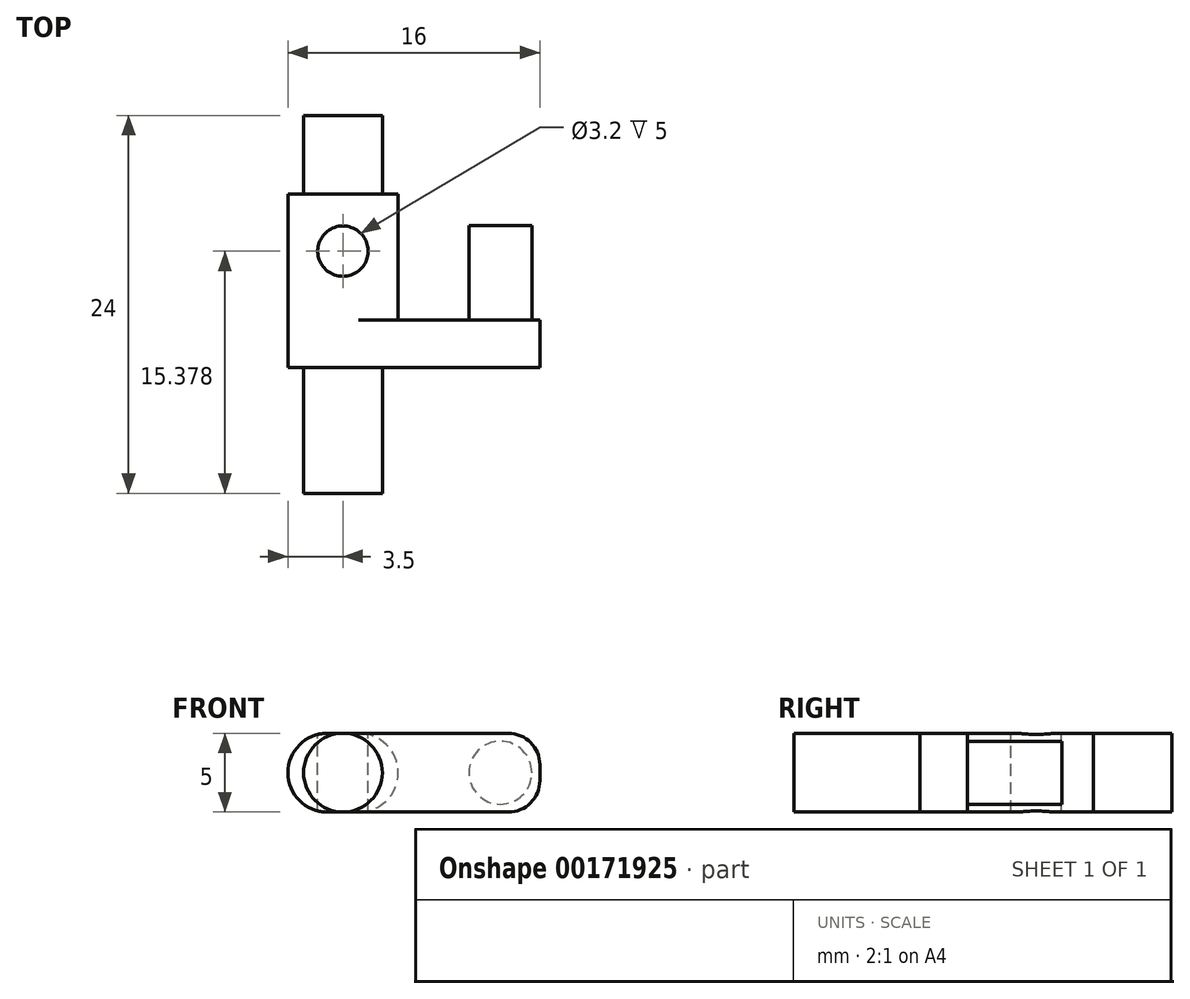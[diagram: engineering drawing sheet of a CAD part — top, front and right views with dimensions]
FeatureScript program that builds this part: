
annotation { "Feature Type Name" : "Feature", "Feature Type Description" : "" }
export const myFeature = defineFeature(function(context is Context, id is Id, definition is map)
    precondition{}
    {
        {
            var Q0;
            Q0=qCreatedBy(makeId("Top.planeOp"),FACE);
            var sketch = newSketch(context, id + "F0", { "sketchPlane" : qUnion([Q0])});
            skLineSegment(sketch, "E0.bottom", {"start": v(-2.5, 0) * mm, "end": v(2.5, 0) * mm});
            skLineSegment(sketch, "E0.top", {"start": v(-2.5, -30) * mm, "end": v(2.5, -30) * mm});
            skLineSegment(sketch, "E0.left", {"start": v(-2.5, 0) * mm, "end": v(-2.5, -30) * mm});
            skLineSegment(sketch, "E0.right", {"start": v(2.5, 0) * mm, "end": v(2.5, -30) * mm});
            skLineSegment(sketch, "E1.bottom", {"start": v(2.5, -14) * mm, "end": v(12.5, -14) * mm});
            skLineSegment(sketch, "E1.top", {"start": v(2.5, -19) * mm, "end": v(12.5, -19) * mm});
            skLineSegment(sketch, "E1.left", {"start": v(2.5, -14) * mm, "end": v(2.5, -19) * mm});
            skLineSegment(sketch, "E1.right", {"start": v(12.5, -14) * mm, "end": v(12.5, -19) * mm});
            skLineSegment(sketch, "E2.bottom", {"start": v(12.5, -14) * mm, "end": v(7.5, -14) * mm});
            skLineSegment(sketch, "E2.top", {"start": v(12.5, -7) * mm, "end": v(7.5, -7) * mm});
            skLineSegment(sketch, "E2.left", {"start": v(12.5, -14) * mm, "end": v(12.5, -7) * mm});
            skLineSegment(sketch, "E2.right", {"start": v(7.5, -14) * mm, "end": v(7.5, -7) * mm});
            skLineSegment(sketch, "E3.bottom", {"start": v(3.5, -7) * mm, "end": v(-3.5, -7) * mm});
            skLineSegment(sketch, "E3.top", {"start": v(3.5, -19) * mm, "end": v(-3.5, -19) * mm});
            skLineSegment(sketch, "E3.left", {"start": v(3.5, -7) * mm, "end": v(3.5, -19) * mm});
            skLineSegment(sketch, "E3.right", {"start": v(-3.5, -7) * mm, "end": v(-3.5, -19) * mm});
            skLineSegment(sketch, "E4", {"start": v(10, -1.58) * mm, "end": v(10, -28.53) * mm, "construction": true});
            skPoint(sketch, "E4.startSnap0", {"position": v(10, -7) * mm});
            skSolve(sketch);
        }
        {
            var Q0;
            Q0 = qSketchRegion(id + "F0", true);
            extrude(context, id + "F1", {"entities" : qUnion([Q0]), "depth" : 5 * mm});
        }
        {
            var Q0;
            Q0=makeQuery(id+"F1.opExtrude","SWEPT_FACE",FACE,{"disambiguationData":[OSD([sQuery(id+"F0.wireOp",EDGE,"E0.bottom")])]});
            var sketch = newSketch(context, id + "F2", { "sketchPlane" : qUnion([Q0])});
            skCircle(sketch, "E5", {"center": v(0, 2.5) * mm, "radius": 2.5 * mm});
            skPoint(sketch, "E5.centerSnap0", {"position": v(2.5, 2.5) * mm});
            skPoint(sketch, "E5.centerSnap1", {"position": v(0, 5) * mm});
            skSolve(sketch);
        }
        {
            var Q0;
            {var subQ0=sQuery(id+"F2.wireOp",EDGE,"E5");var subQ1=sQuery(id+"F0.wireOp",EDGE,"E0.bottom");var subQ4=makeQuery(id+"F1.opExtrude","CAP_EDGE",EDGE,{"disambiguationData":[OSD([subQ1])],"isStart":true});var subQ5=makeQuery(id+"F2.imprint","INTERSECT",VERTEX,{"derivedFrom":[subQ4,subQ0]});Q0=makeQuery(id+"F2.imprint","IMPRINT",FACE,{"disambiguationData":[TD([[makeQuery(id+"F2.imprint","IMPRINT",EDGE,{"disambiguationData":[TD([[subQ5,1.0]])],"derivedFrom":subQ0}),-1.0]])]});}
            var Q1;
            {var subQ0=sQuery(id+"F2.wireOp",EDGE,"E5");var subQ1=sQuery(id+"F0.wireOp",EDGE,"E0.bottom");var subQ2=makeQuery(id+"F1.opExtrude","CAP_EDGE",EDGE,{"disambiguationData":[OSD([subQ1])],"isStart":false});var subQ3=makeQuery(id+"F2.imprint","INTERSECT",VERTEX,{"derivedFrom":[subQ2,subQ0]});Q1=makeQuery(id+"F2.imprint","IMPRINT",FACE,{"disambiguationData":[TD([[makeQuery(id+"F2.imprint","IMPRINT",EDGE,{"disambiguationData":[TD([[subQ3,-1.0]])],"derivedFrom":subQ0}),-1.0]])]});}
            var Q2;
            {var subQ0=sQuery(id+"F2.wireOp",EDGE,"E5");var subQ1=sQuery(id+"F0.wireOp",EDGE,"E0.bottom");var subQ2=makeQuery(id+"F1.opExtrude","CAP_EDGE",EDGE,{"disambiguationData":[OSD([subQ1])],"isStart":false});var subQ3=makeQuery(id+"F2.imprint","INTERSECT",VERTEX,{"derivedFrom":[subQ2,subQ0]});Q2=makeQuery(id+"F2.imprint","IMPRINT",FACE,{"disambiguationData":[TD([[makeQuery(id+"F2.imprint","IMPRINT",EDGE,{"disambiguationData":[TD([[subQ3,1.0]])],"derivedFrom":subQ0}),-1.0]])]});}
            var Q3;
            {var subQ0=sQuery(id+"F2.wireOp",EDGE,"E5");var subQ1=sQuery(id+"F0.wireOp",EDGE,"E0.bottom");var subQ4=makeQuery(id+"F1.opExtrude","CAP_EDGE",EDGE,{"disambiguationData":[OSD([subQ1])],"isStart":true});var subQ5=makeQuery(id+"F2.imprint","INTERSECT",VERTEX,{"derivedFrom":[subQ4,subQ0]});Q3=makeQuery(id+"F2.imprint","IMPRINT",FACE,{"disambiguationData":[TD([[makeQuery(id+"F2.imprint","IMPRINT",EDGE,{"disambiguationData":[TD([[subQ5,-1.0]])],"derivedFrom":subQ0}),-1.0]])]});}
            var Q4;
            {var subQ0=sQuery(id+"F0.wireOp",EDGE,"E3.bottom");Q4=makeQuery(id+"F1.opExtrude","SWEPT_FACE",FACE,{"disambiguationData":[OSD([subQ0]),TDD([makeQuery(id+"F0.imprint","IMPRINT",EDGE,{"disambiguationData":[TD([[makeQuery(id+"F0.imprint","INTERSECT",VERTEX,{"derivedFrom":[subQ0,sQuery(id+"F0.wireOp",EDGE,"E3.left")]}),-1.0]])],"derivedFrom":subQ0})])]});}
            extrude(context, id + "F3", {"entities" : qUnion([Q0, Q1, Q2, Q3]), "operationType" : NewBodyOperationType.REMOVE, "endBound" : BoundingType.UP_TO_SURFACE, "oppositeDirection" : true, "endBoundEntityFace" : qUnion([Q4]), "depth" : 5.05 * mm});
        }
        {
            var Q0;
            Q0=makeQuery(id+"F1.opExtrude","SWEPT_FACE",FACE,{"disambiguationData":[OSD([sQuery(id+"F0.wireOp",EDGE,"E0.top")])]});
            var sketch = newSketch(context, id + "F4", { "sketchPlane" : qUnion([Q0])});
            skCircle(sketch, "E6", {"center": v(0, 2.5) * mm, "radius": 2.5 * mm});
            skPoint(sketch, "E6.centerSnap0", {"position": v(-2.5, 2.5) * mm});
            skSolve(sketch);
        }
        {
            var Q0;
            {var subQ0=sQuery(id+"F4.wireOp",EDGE,"E6");var subQ1=sQuery(id+"F0.wireOp",EDGE,"E0.top");var subQ2=makeQuery(id+"F1.opExtrude","CAP_EDGE",EDGE,{"disambiguationData":[OSD([subQ1])],"isStart":false});var subQ3=makeQuery(id+"F4.imprint","INTERSECT",VERTEX,{"derivedFrom":[subQ2,subQ0]});Q0=makeQuery(id+"F4.imprint","IMPRINT",FACE,{"disambiguationData":[TD([[makeQuery(id+"F4.imprint","IMPRINT",EDGE,{"disambiguationData":[TD([[subQ3,1.0]])],"derivedFrom":subQ0}),-1.0]])]});}
            var Q1;
            {var subQ0=sQuery(id+"F4.wireOp",EDGE,"E6");var subQ1=sQuery(id+"F0.wireOp",EDGE,"E0.top");var subQ4=makeQuery(id+"F1.opExtrude","CAP_EDGE",EDGE,{"disambiguationData":[OSD([subQ1])],"isStart":true});var subQ5=makeQuery(id+"F4.imprint","INTERSECT",VERTEX,{"derivedFrom":[subQ4,subQ0]});Q1=makeQuery(id+"F4.imprint","IMPRINT",FACE,{"disambiguationData":[TD([[makeQuery(id+"F4.imprint","IMPRINT",EDGE,{"disambiguationData":[TD([[subQ5,-1.0]])],"derivedFrom":subQ0}),-1.0]])]});}
            var Q2;
            {var subQ0=sQuery(id+"F4.wireOp",EDGE,"E6");var subQ1=sQuery(id+"F0.wireOp",EDGE,"E0.top");var subQ4=makeQuery(id+"F1.opExtrude","CAP_EDGE",EDGE,{"disambiguationData":[OSD([subQ1])],"isStart":true});var subQ5=makeQuery(id+"F4.imprint","INTERSECT",VERTEX,{"derivedFrom":[subQ4,subQ0]});Q2=makeQuery(id+"F4.imprint","IMPRINT",FACE,{"disambiguationData":[TD([[makeQuery(id+"F4.imprint","IMPRINT",EDGE,{"disambiguationData":[TD([[subQ5,1.0]])],"derivedFrom":subQ0}),-1.0]])]});}
            var Q3;
            {var subQ0=sQuery(id+"F4.wireOp",EDGE,"E6");var subQ1=sQuery(id+"F0.wireOp",EDGE,"E0.top");var subQ2=makeQuery(id+"F1.opExtrude","CAP_EDGE",EDGE,{"disambiguationData":[OSD([subQ1])],"isStart":false});var subQ3=makeQuery(id+"F4.imprint","INTERSECT",VERTEX,{"derivedFrom":[subQ2,subQ0]});Q3=makeQuery(id+"F4.imprint","IMPRINT",FACE,{"disambiguationData":[TD([[makeQuery(id+"F4.imprint","IMPRINT",EDGE,{"disambiguationData":[TD([[subQ3,-1.0]])],"derivedFrom":subQ0}),-1.0]])]});}
            var Q4;
            Q4=makeQuery(id+"F1.opExtrude","SWEPT_FACE",FACE,{"disambiguationData":[OSD([sQuery(id+"F0.wireOp",EDGE,"E1.top"),sQuery(id+"F0.wireOp",EDGE,"E3.top")])]});
            extrude(context, id + "F5", {"entities" : qUnion([Q0, Q1, Q2, Q3]), "operationType" : NewBodyOperationType.REMOVE, "endBound" : BoundingType.UP_TO_SURFACE, "oppositeDirection" : true, "endBoundEntityFace" : qUnion([Q4]), "depth" : 25 * mm});
        }
        {
            var Q0;
            Q0=makeQuery(id+"F1.opExtrude","SWEPT_FACE",FACE,{"disambiguationData":[OSD([sQuery(id+"F0.wireOp",EDGE,"E2.top")])]});
            var sketch = newSketch(context, id + "F6", { "sketchPlane" : qUnion([Q0])});
            skCircle(sketch, "E7", {"center": v(-10, 2.5) * mm, "radius": 2.5 * mm});
            skPoint(sketch, "E7.centerSnap0", {"position": v(-10, 5) * mm});
            skPoint(sketch, "E7.centerSnap1", {"position": v(-7.5, 2.5) * mm});
            skSolve(sketch);
        }
        {
            var Q0;
            {var subQ0=sQuery(id+"F6.wireOp",EDGE,"E7");var subQ1=sQuery(id+"F0.wireOp",EDGE,"E2.top");var subQ4=makeQuery(id+"F1.opExtrude","CAP_EDGE",EDGE,{"disambiguationData":[OSD([subQ1])],"isStart":true});var subQ5=makeQuery(id+"F6.imprint","INTERSECT",VERTEX,{"derivedFrom":[subQ4,subQ0]});Q0=makeQuery(id+"F6.imprint","IMPRINT",FACE,{"disambiguationData":[TD([[makeQuery(id+"F6.imprint","IMPRINT",EDGE,{"disambiguationData":[TD([[subQ5,1.0]])],"derivedFrom":subQ0}),-1.0]])]});}
            var Q1;
            {var subQ0=sQuery(id+"F6.wireOp",EDGE,"E7");var subQ1=sQuery(id+"F0.wireOp",EDGE,"E2.top");var subQ4=makeQuery(id+"F1.opExtrude","CAP_EDGE",EDGE,{"disambiguationData":[OSD([subQ1])],"isStart":true});var subQ5=makeQuery(id+"F6.imprint","INTERSECT",VERTEX,{"derivedFrom":[subQ4,subQ0]});Q1=makeQuery(id+"F6.imprint","IMPRINT",FACE,{"disambiguationData":[TD([[makeQuery(id+"F6.imprint","IMPRINT",EDGE,{"disambiguationData":[TD([[subQ5,-1.0]])],"derivedFrom":subQ0}),-1.0]])]});}
            var Q2;
            {var subQ0=sQuery(id+"F6.wireOp",EDGE,"E7");var subQ1=sQuery(id+"F0.wireOp",EDGE,"E2.top");var subQ2=makeQuery(id+"F1.opExtrude","CAP_EDGE",EDGE,{"disambiguationData":[OSD([subQ1])],"isStart":false});var subQ3=makeQuery(id+"F6.imprint","INTERSECT",VERTEX,{"derivedFrom":[subQ2,subQ0]});Q2=makeQuery(id+"F6.imprint","IMPRINT",FACE,{"disambiguationData":[TD([[makeQuery(id+"F6.imprint","IMPRINT",EDGE,{"disambiguationData":[TD([[subQ3,1.0]])],"derivedFrom":subQ0}),-1.0]])]});}
            var Q3;
            {var subQ0=sQuery(id+"F6.wireOp",EDGE,"E7");var subQ1=sQuery(id+"F0.wireOp",EDGE,"E2.top");var subQ2=makeQuery(id+"F1.opExtrude","CAP_EDGE",EDGE,{"disambiguationData":[OSD([subQ1])],"isStart":false});var subQ3=makeQuery(id+"F6.imprint","INTERSECT",VERTEX,{"derivedFrom":[subQ2,subQ0]});Q3=makeQuery(id+"F6.imprint","IMPRINT",FACE,{"disambiguationData":[TD([[makeQuery(id+"F6.imprint","IMPRINT",EDGE,{"disambiguationData":[TD([[subQ3,-1.0]])],"derivedFrom":subQ0}),-1.0]])]});}
            var Q4;
            Q4=makeQuery(id+"F1.opExtrude","SWEPT_FACE",FACE,{"disambiguationData":[OSD([sQuery(id+"F0.wireOp",EDGE,"E1.bottom")])]});
            extrude(context, id + "F7", {"entities" : qUnion([Q0, Q1, Q2, Q3]), "operationType" : NewBodyOperationType.REMOVE, "endBound" : BoundingType.UP_TO_SURFACE, "oppositeDirection" : true, "endBoundEntityFace" : qUnion([Q4]), "depth" : 25 * mm});
        }
        {
            var Q0;
            Q0=makeQuery(id+"F1.opExtrude","CAP_EDGE",EDGE,{"disambiguationData":[OSD([sQuery(id+"F0.wireOp",EDGE,"E1.right"),sQuery(id+"F0.wireOp",EDGE,"E2.left")])],"isStart":true});
            var Q1;
            Q1=makeQuery(id+"F1.opExtrude","CAP_EDGE",EDGE,{"disambiguationData":[OSD([sQuery(id+"F0.wireOp",EDGE,"E1.right"),sQuery(id+"F0.wireOp",EDGE,"E2.left")])],"isStart":false});
            fillet(context, id + "F8", {"entities" : qUnion([Q0, Q1]), "radius" : 2 * mm, "tangentPropagation" : true, "allowEdgeOverflow" : false});
        }
        {
            var Q0;
            Q0=makeQuery(id+"F1.opExtrude","CAP_FACE",FACE,{"disambiguationData":[OSD([sQuery(id+"F0.wireOp",EDGE,"E0.bottom"),sQuery(id+"F0.wireOp",EDGE,"E0.top"),sQuery(id+"F0.wireOp",EDGE,"E0.left"),sQuery(id+"F0.wireOp",EDGE,"E0.right"),sQuery(id+"F0.wireOp",EDGE,"E1.bottom"),sQuery(id+"F0.wireOp",EDGE,"E1.top"),sQuery(id+"F0.wireOp",EDGE,"E1.right"),sQuery(id+"F0.wireOp",EDGE,"E2.top"),sQuery(id+"F0.wireOp",EDGE,"E2.left"),sQuery(id+"F0.wireOp",EDGE,"E2.right"),sQuery(id+"F0.wireOp",EDGE,"E3.bottom"),sQuery(id+"F0.wireOp",EDGE,"E3.top"),sQuery(id+"F0.wireOp",EDGE,"E3.left"),sQuery(id+"F0.wireOp",EDGE,"E3.right")])],"isStart":false});
            var sketch = newSketch(context, id + "F9", { "sketchPlane" : qUnion([Q0])});
            skCircle(sketch, "E8", {"center": v(0, -10.62) * mm, "radius": 1.6 * mm});
            skSolve(sketch);
        }
        {
            var Q0;
            Q0 = qSketchRegion(id + "F9", true);
            extrude(context, id + "F10", {"entities" : qUnion([Q0]), "operationType" : NewBodyOperationType.REMOVE, "oppositeDirection" : true, "depth" : 25 * mm});
        }
        {
            var Q0;
            Q0=makeQuery(id+"F1.opExtrude","CAP_EDGE",EDGE,{"disambiguationData":[OSD([sQuery(id+"F0.wireOp",EDGE,"E3.right")])],"isStart":false});
            var Q1;
            Q1=makeQuery(id+"F1.opExtrude","CAP_EDGE",EDGE,{"disambiguationData":[OSD([sQuery(id+"F0.wireOp",EDGE,"E3.right")])],"isStart":true});
            var Q2;
            Q2=makeQuery(id+"F1.opExtrude","CAP_EDGE",EDGE,{"disambiguationData":[OSD([sQuery(id+"F0.wireOp",EDGE,"E3.left")])],"isStart":false});
            var Q3;
            Q3=makeQuery(id+"F1.opExtrude","CAP_EDGE",EDGE,{"disambiguationData":[OSD([sQuery(id+"F0.wireOp",EDGE,"E3.left")])],"isStart":true});
            fillet(context, id + "F11", {"entities" : qUnion([Q0, Q1, Q2, Q3]), "radius" : 2.5 * mm, "tangentPropagation" : true, "allowEdgeOverflow" : false});
        }
        {
            var Q0;
            Q0=makeQuery(id+"F1.opExtrude","SWEPT_FACE",FACE,{"disambiguationData":[OSD([sQuery(id+"F0.wireOp",EDGE,"E0.bottom")])]});
            extrude(context, id + "F12", {"entities" : qUnion([Q0]), "operationType" : NewBodyOperationType.REMOVE, "oppositeDirection" : true, "depth" : 4 * mm});
        }
        {
            var Q0;
            Q0=makeQuery(id+"F1.opExtrude","SWEPT_FACE",FACE,{"disambiguationData":[OSD([sQuery(id+"F0.wireOp",EDGE,"E0.top")])]});
            extrude(context, id + "F13", {"entities" : qUnion([Q0]), "operationType" : NewBodyOperationType.REMOVE, "oppositeDirection" : true, "depth" : 5 * mm});
        }
        {
            var Q0;
            Q0=makeQuery(id+"F1.opExtrude","SWEPT_FACE",FACE,{"disambiguationData":[OSD([sQuery(id+"F0.wireOp",EDGE,"E2.top")])]});
            var sketch = newSketch(context, id + "F14", { "sketchPlane" : qUnion([Q0])});
            skCircle(sketch, "E9", {"center": v(-10, 2.5) * mm, "radius": 2 * mm});
            skSolve(sketch);
        }
        {
            var Q0;
            Q0=makeQuery(id+"F14.imprint","IMPRINT",FACE,{"disambiguationData":[TD([[makeQuery(id+"F14.imprint","IMPRINT",EDGE,{"derivedFrom":sQuery(id+"F14.wireOp",EDGE,"E9")}),-1.0]])]});
            var Q1;
            {var subQ0=sQuery(id+"F6.wireOp",EDGE,"E7");var subQ1=sQuery(id+"F0.wireOp",EDGE,"E2.top");var subQ3=sQuery(id+"F0.wireOp",EDGE,"E1.bottom");Q1=makeQuery(id+"F7.boolean.opBoolean","MERGE",FACE,{"derivedFrom":[makeQuery(id+"F1.opExtrude","SWEPT_FACE",FACE,{"disambiguationData":[OSD([subQ3])]}),makeQuery(id+"F7.opExtrude","CAP_FACE",FACE,{"disambiguationData":[OSD([subQ3]),ownerDisambiguation([makeQuery(id+"F6.imprint","IMPRINT",EDGE,{"disambiguationData":[TD([[makeQuery(id+"F6.imprint","INTERSECT",VERTEX,{"derivedFrom":[makeQuery(id+"F1.opExtrude","CAP_EDGE",EDGE,{"disambiguationData":[OSD([subQ1])],"isStart":false}),subQ0]}),1.0]])],"derivedFrom":subQ0})])],"isStart":false}),makeQuery(id+"F7.opExtrude","CAP_FACE",FACE,{"disambiguationData":[OSD([subQ3]),ownerDisambiguation([makeQuery(id+"F6.imprint","IMPRINT",EDGE,{"disambiguationData":[TD([[makeQuery(id+"F6.imprint","INTERSECT",VERTEX,{"derivedFrom":[makeQuery(id+"F1.opExtrude","CAP_EDGE",EDGE,{"disambiguationData":[OSD([subQ1])],"isStart":true}),subQ0]}),-1.0]])],"derivedFrom":subQ0})])],"isStart":false})]});}
            extrude(context, id + "F15", {"entities" : qUnion([Q0]), "operationType" : NewBodyOperationType.REMOVE, "endBound" : BoundingType.UP_TO_SURFACE, "oppositeDirection" : true, "endBoundEntityFace" : qUnion([Q1]), "depth" : 25 * mm});
        }
        {
            var Q0;
            Q0=makeQuery(id+"F1.opExtrude","SWEPT_FACE",FACE,{"disambiguationData":[OSD([sQuery(id+"F0.wireOp",EDGE,"E2.top")])]});
            extrude(context, id + "F16", {"entities" : qUnion([Q0]), "operationType" : NewBodyOperationType.REMOVE, "oppositeDirection" : true, "depth" : 2 * mm});
        }
        {
            var Q0;
            Q0=makeQuery(id+"F12.boolean.opBoolean","COPY",FACE,{"derivedFrom":makeQuery(id+"F12.opExtrude","CAP_FACE",FACE,{"disambiguationData":[OSD([sQuery(id+"F0.wireOp",EDGE,"E0.bottom")])],"isStart":false})});
            extrude(context, id + "F17", {"entities" : qUnion([Q0]), "operationType" : NewBodyOperationType.ADD, "depth" : 2 * mm});
        }
        {
            var Q0;
            Q0=makeQuery(id+"F13.boolean.opBoolean","COPY",FACE,{"derivedFrom":makeQuery(id+"F13.opExtrude","CAP_FACE",FACE,{"disambiguationData":[OSD([sQuery(id+"F0.wireOp",EDGE,"E0.top")])],"isStart":false})});
            extrude(context, id + "F18", {"entities" : qUnion([Q0]), "operationType" : NewBodyOperationType.ADD, "depth" : 1 * mm});
        }
        {
            var Q0;
            {var subQ0=sQuery(id+"F4.wireOp",EDGE,"E6");var subQ1=sQuery(id+"F0.wireOp",EDGE,"E0.top");var subQ3=sQuery(id+"F0.wireOp",EDGE,"E3.top");var subQ4=sQuery(id+"F0.wireOp",EDGE,"E1.top");Q0=makeQuery(id+"F5.boolean.opBoolean","MERGE",FACE,{"derivedFrom":[makeQuery(id+"F1.opExtrude","SWEPT_FACE",FACE,{"disambiguationData":[OSD([subQ4,subQ3])]}),makeQuery(id+"F5.opExtrude","CAP_FACE",FACE,{"disambiguationData":[OSD([subQ4,subQ3]),ownerDisambiguation([makeQuery(id+"F4.imprint","IMPRINT",EDGE,{"disambiguationData":[TD([[makeQuery(id+"F4.imprint","INTERSECT",VERTEX,{"derivedFrom":[makeQuery(id+"F1.opExtrude","CAP_EDGE",EDGE,{"disambiguationData":[OSD([subQ1])],"isStart":false}),subQ0]}),1.0]])],"derivedFrom":subQ0})])],"isStart":false}),makeQuery(id+"F5.opExtrude","CAP_FACE",FACE,{"disambiguationData":[OSD([subQ4,subQ3]),ownerDisambiguation([makeQuery(id+"F4.imprint","IMPRINT",EDGE,{"disambiguationData":[TD([[makeQuery(id+"F4.imprint","INTERSECT",VERTEX,{"derivedFrom":[makeQuery(id+"F1.opExtrude","CAP_EDGE",EDGE,{"disambiguationData":[OSD([subQ1])],"isStart":true}),subQ0]}),-1.0]])],"derivedFrom":subQ0})])],"isStart":false})]});}
            var Q1;
            {var subQ0=sQuery(id+"F4.wireOp",EDGE,"E6");var subQ1=sQuery(id+"F0.wireOp",EDGE,"E0.top");var subQ3=sQuery(id+"F0.wireOp",EDGE,"E3.top");var subQ4=sQuery(id+"F0.wireOp",EDGE,"E1.top");Q1=makeQuery(id+"F5.boolean.opBoolean","MERGE",FACE,{"derivedFrom":[makeQuery(id+"F1.opExtrude","SWEPT_FACE",FACE,{"disambiguationData":[OSD([subQ3])]}),makeQuery(id+"F5.opExtrude","CAP_FACE",FACE,{"disambiguationData":[OSD([subQ4,subQ3]),ownerDisambiguation([makeQuery(id+"F4.imprint","IMPRINT",EDGE,{"disambiguationData":[TD([[makeQuery(id+"F4.imprint","INTERSECT",VERTEX,{"derivedFrom":[makeQuery(id+"F1.opExtrude","CAP_EDGE",EDGE,{"disambiguationData":[OSD([subQ1])],"isStart":false}),subQ0]}),-1.0]])],"derivedFrom":subQ0})])],"isStart":false}),makeQuery(id+"F5.opExtrude","CAP_FACE",FACE,{"disambiguationData":[OSD([subQ4,subQ3]),ownerDisambiguation([makeQuery(id+"F4.imprint","IMPRINT",EDGE,{"disambiguationData":[TD([[makeQuery(id+"F4.imprint","INTERSECT",VERTEX,{"derivedFrom":[makeQuery(id+"F1.opExtrude","CAP_EDGE",EDGE,{"disambiguationData":[OSD([subQ1])],"isStart":true}),subQ0]}),1.0]])],"derivedFrom":subQ0})])],"isStart":false})]});}
            extrude(context, id + "F19", {"entities" : qUnion([Q0, Q1]), "operationType" : NewBodyOperationType.REMOVE, "oppositeDirection" : true, "depth" : 1 * mm});
        }
        {
            var Q0;
            {var subQ0=sQuery(id+"F0.wireOp",EDGE,"E1.bottom");Q0=makeQuery(id+"F15.boolean.opBoolean","MERGE",FACE,{"derivedFrom":[makeQuery(id+"F7.boolean.opBoolean","COPY",FACE,{"derivedFrom":makeQuery(id+"F7.opExtrude","CAP_FACE",FACE,{"disambiguationData":[OSD([subQ0]),OD(1.0)],"isStart":false})}),makeQuery(id+"F7.boolean.opBoolean","COPY",FACE,{"derivedFrom":makeQuery(id+"F7.opExtrude","CAP_FACE",FACE,{"disambiguationData":[OSD([subQ0]),OD(2.0)],"isStart":false})}),makeQuery(id+"F7.boolean.opBoolean","MERGE",FACE,{"derivedFrom":[makeQuery(id+"F1.opExtrude","SWEPT_FACE",FACE,{"disambiguationData":[OSD([subQ0])]}),makeQuery(id+"F7.opExtrude","CAP_FACE",FACE,{"disambiguationData":[OSD([subQ0]),OD(0.0)],"isStart":false}),makeQuery(id+"F7.opExtrude","CAP_FACE",FACE,{"disambiguationData":[OSD([subQ0]),OD(3.0)],"isStart":false})]})],"fromTools":[makeQuery(id+"F15.opExtrude","CAP_FACE",FACE,{"disambiguationData":[OSD([sQuery(id+"F6.wireOp",EDGE,"E7"),sQuery(id+"F14.wireOp",EDGE,"E9")])],"isStart":false})]});}
            extrude(context, id + "F20", {"entities" : qUnion([Q0]), "operationType" : NewBodyOperationType.REMOVE, "oppositeDirection" : true, "depth" : 1 * mm});
        }
    });
